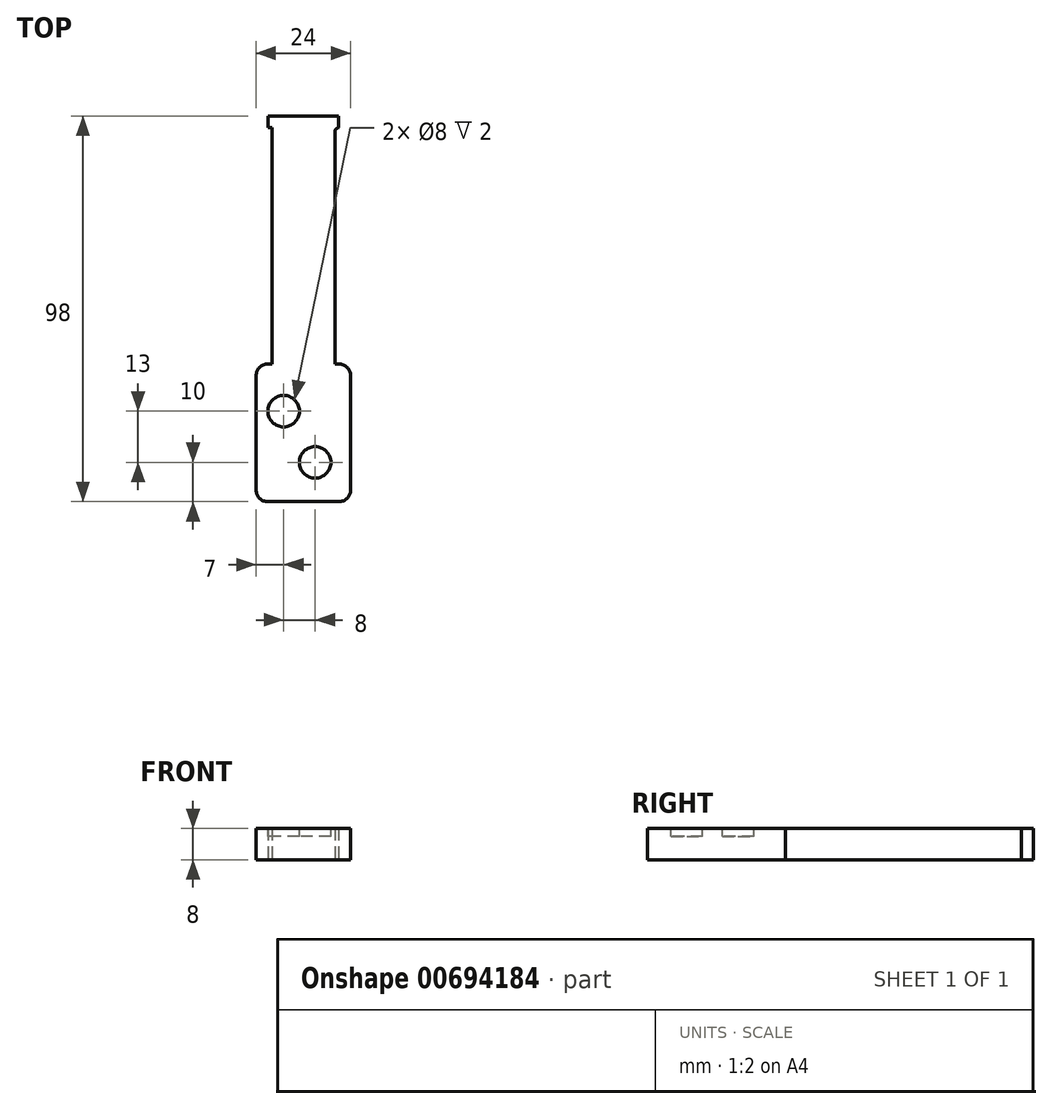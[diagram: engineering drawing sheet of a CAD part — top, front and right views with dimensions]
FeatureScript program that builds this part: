
annotation { "Feature Type Name" : "Feature", "Feature Type Description" : "" }
export const myFeature = defineFeature(function(context is Context, id is Id, definition is map)
    precondition{}
    {
        {
            var Q0;
            Q0=qCreatedBy(makeId("Front.planeOp"),FACE);
            var sketch = newSketch(context, id + "F0", { "sketchPlane" : qUnion([Q0])});
            skLineSegment(sketch, "E0.bottom", {"start": v(-9, 4) * mm, "end": v(9, 4) * mm});
            skLineSegment(sketch, "E0.top", {"start": v(-9, -4) * mm, "end": v(9, -4) * mm});
            skLineSegment(sketch, "E0.left", {"start": v(-9, 4) * mm, "end": v(-9, -4) * mm});
            skLineSegment(sketch, "E0.right", {"start": v(9, 4) * mm, "end": v(9, -4) * mm});
            skSolve(sketch);
        }
        {
            var Q0;
            Q0=makeQuery(id+"F0.imprint","IMPRINT",FACE,{"disambiguationData":[TD([[makeQuery(id+"F0.imprint","IMPRINT",EDGE,{"derivedFrom":sQuery(id+"F0.wireOp",EDGE,"E0.bottom")}),-1.0]])]});
            extrude(context, id + "F1", {"entities" : qUnion([Q0]), "depth" : 3 * mm, "offsetDistance" : 25 * mm});
        }
        {
            var Q0;
            Q0=makeQuery(id+"F1.opExtrude","CAP_FACE",FACE,{"disambiguationData":[OSD([sQuery(id+"F0.wireOp",EDGE,"E0.bottom"),sQuery(id+"F0.wireOp",EDGE,"E0.top"),sQuery(id+"F0.wireOp",EDGE,"E0.left"),sQuery(id+"F0.wireOp",EDGE,"E0.right")])],"isStart":false});
            var sketch = newSketch(context, id + "F2", { "sketchPlane" : qUnion([Q0])});
            skLineSegment(sketch, "E1.bottom", {"start": v(-8, 4) * mm, "end": v(8, 4) * mm});
            skLineSegment(sketch, "E1.top", {"start": v(-8, -4) * mm, "end": v(8, -4) * mm});
            skLineSegment(sketch, "E1.left", {"start": v(-8, 4) * mm, "end": v(-8, -4) * mm});
            skLineSegment(sketch, "E1.right", {"start": v(8, 4) * mm, "end": v(8, -4) * mm});
            skSolve(sketch);
        }
        {
            var Q0;
            Q0 = qSketchRegion(id + "F2", true);
            extrude(context, id + "F3", {"entities" : qUnion([Q0]), "operationType" : NewBodyOperationType.ADD, "depth" : 60 * mm, "offsetDistance" : 25 * mm});
        }
        {
            var Q0;
            Q0=makeQuery(id+"F3.opExtrude","CAP_EDGE",EDGE,{"disambiguationData":[OSD([sQuery(id+"F2.wireOp",EDGE,"E1.left")])],"isStart":true});
            var Q1;
            Q1=makeQuery(id+"F3.opExtrude","CAP_EDGE",EDGE,{"disambiguationData":[OSD([sQuery(id+"F2.wireOp",EDGE,"E1.right")])],"isStart":true});
            fillet(context, id + "F4", {"entities" : qUnion([Q0, Q1]), "radius" : 1 * mm, "tangentPropagation" : true, "allowEdgeOverflow" : false});
        }
        {
            var Q0;
            Q0=makeQuery(id+"F3.opExtrude","CAP_FACE",FACE,{"disambiguationData":[OSD([sQuery(id+"F2.wireOp",EDGE,"E1.bottom"),sQuery(id+"F2.wireOp",EDGE,"E1.top"),sQuery(id+"F2.wireOp",EDGE,"E1.left"),sQuery(id+"F2.wireOp",EDGE,"E1.right")])],"isStart":false});
            var sketch = newSketch(context, id + "F5", { "sketchPlane" : qUnion([Q0])});
            skLineSegment(sketch, "E2.bottom", {"start": v(-12, 4) * mm, "end": v(12, 4) * mm});
            skLineSegment(sketch, "E2.top", {"start": v(-12, -4) * mm, "end": v(12, -4) * mm});
            skLineSegment(sketch, "E2.left", {"start": v(-12, 4) * mm, "end": v(-12, -4) * mm});
            skLineSegment(sketch, "E2.right", {"start": v(12, 4) * mm, "end": v(12, -4) * mm});
            skSolve(sketch);
        }
        {
            var Q0;
            Q0 = qSketchRegion(id + "F5", true);
            extrude(context, id + "F6", {"entities" : qUnion([Q0]), "operationType" : NewBodyOperationType.ADD, "depth" : 35 * mm, "offsetDistance" : 25 * mm});
        }
        {
            var Q0;
            Q0=makeQuery(id+"F6.opExtrude","CAP_EDGE",EDGE,{"disambiguationData":[OSD([sQuery(id+"F5.wireOp",EDGE,"E2.left")])],"isStart":true});
            var Q1;
            Q1=makeQuery(id+"F6.opExtrude","CAP_EDGE",EDGE,{"disambiguationData":[OSD([sQuery(id+"F5.wireOp",EDGE,"E2.left")])],"isStart":false});
            var Q2;
            Q2=makeQuery(id+"F6.opExtrude","CAP_EDGE",EDGE,{"disambiguationData":[OSD([sQuery(id+"F5.wireOp",EDGE,"E2.right")])],"isStart":false});
            var Q3;
            Q3=makeQuery(id+"F6.opExtrude","CAP_EDGE",EDGE,{"disambiguationData":[OSD([sQuery(id+"F5.wireOp",EDGE,"E2.right")])],"isStart":true});
            fillet(context, id + "F7", {"entities" : qUnion([Q0, Q1, Q2, Q3]), "radius" : 3 * mm, "tangentPropagation" : true, "allowEdgeOverflow" : false});
        }
        {
            var Q0;
            Q0=makeQuery(id+"F6.boolean.opBoolean","MERGE",FACE,{"derivedFrom":[makeQuery(id+"F3.boolean.opBoolean","MERGE",FACE,{"derivedFrom":[makeQuery(id+"F1.opExtrude","SWEPT_FACE",FACE,{"disambiguationData":[OSD([sQuery(id+"F0.wireOp",EDGE,"E0.bottom")])]}),makeQuery(id+"F3.opExtrude","SWEPT_FACE",FACE,{"disambiguationData":[OSD([sQuery(id+"F2.wireOp",EDGE,"E1.bottom")])]})]}),makeQuery(id+"F6.opExtrude","SWEPT_FACE",FACE,{"disambiguationData":[OSD([sQuery(id+"F5.wireOp",EDGE,"E2.bottom")])]})]});
            var sketch = newSketch(context, id + "F8", { "sketchPlane" : qUnion([Q0])});
            skCircle(sketch, "E3", {"center": v(-5, -75) * mm, "radius": 4 * mm});
            skCircle(sketch, "E4", {"center": v(3, -88) * mm, "radius": 4 * mm});
            skSolve(sketch);
        }
        {
            var Q0;
            Q0 = qSketchRegion(id + "F8", true);
            extrude(context, id + "F9", {"entities" : qUnion([Q0]), "operationType" : NewBodyOperationType.REMOVE, "oppositeDirection" : true, "depth" : 2 * mm, "offsetDistance" : 25 * mm});
        }
    });
